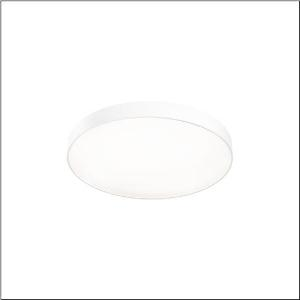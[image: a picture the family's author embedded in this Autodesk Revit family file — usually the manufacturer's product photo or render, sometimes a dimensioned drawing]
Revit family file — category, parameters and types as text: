
# Revit family: round_21_m_51mr36fd0321w
name_source: partatom
category: Lighting Fixtures
units: mm (PartAtom-declared; Revit-internal decimal feet)

## family parameters
Cut with Voids When Loaded = No
Host = Face
Light Source = No
Part Type = Normal
Room Calculation Point = No
Round Connector Dimension = Use Diameter
Shared = No

## types (1)
- Round 21 M (1 x LED, 7500 lm, 54.9 W, 3000K)
    Apparent Load = 55 VA
    CIE Flux Codes = 49 80 96 100 100
    Color Rendering = 80
    Color Temperature = 3000K
    Default Elevation = 1800 mm
    Description = Round 21 M, wall and ceiling luminaire, primary optical cover: cover, of PMMA, opal, light emission: direct distribution, primary light characteristic: symmetric, installation type: suspended mounting, surface-mounted, LED, rated luminous flux: 7.500lm, luminous efficacy: 137lm/W, light colour: 830, colour temperature: 3000K, control gear: DALI 2, with terminal, 5-pole, mains connection: 230V, AC, 50/60Hz, rated input power: 54.8W, housing, of aluminium, coated, white, diameter: 600mm, height: 62mm, protection rating (complete): IP40, insulation class (complete): insulation class I (protective earthing), certification: CE, impact resistance: IK04, permissible operating ambient temperature: -10..+35°C, packaging unit: 1 piece
    Height = 87 mm
    Lamp = 1 x LED
    Lamp Light Flux = 7500 lm
    Lamp Power = 54.9 W
    Lamp count = 1
    Length = 600 mm
    Luminous efficacy = 137 lm/W
    Manufacturer = Siteco
    ModVariant = No
    Model = 51MR36FD0321W
    Mounting Place = Ceiling
    Mounting Type = Surface mounted
    Number of Poles = 1
    OnlyDefault = Yes
    Power Factor = 1
    Product Name = Round 21 M
    Product group = wall and ceiling luminaire | ceiling mounted
    ProductGroupID = 304
    Protection Class = Protection class I
    Protection Degree = IP 40
    RLX_Detail_Level = 1
    RLX_Emergency_Light_Flux = 0 lm
    RLX_Emergency_Type = 0
    RLX_Emergency_Type_DB = No
    RlxData = <blob elided: 11745 chars, md5=11e1c275>
    Socket = socket
    Standby Power = 0 W
    System Light Flux = 7500 lm
    System Power = 55 W
    Type Comments = Product without accessories
    Type Image = l_1258330.jpg
    URL = http://relux.com
    VarID = ---
    Voltage = 0 V
    Weight = 0.00 kg
    Width = 0 mm  [stored 0 ft]

note: [stored X ft] marks values corroborated as IEEE doubles in the binary element streams (Revit-internal decimal feet)

## geometry (parser evidence)
native form markers: Sweep x9
no freeform markers — native parametric forms only
